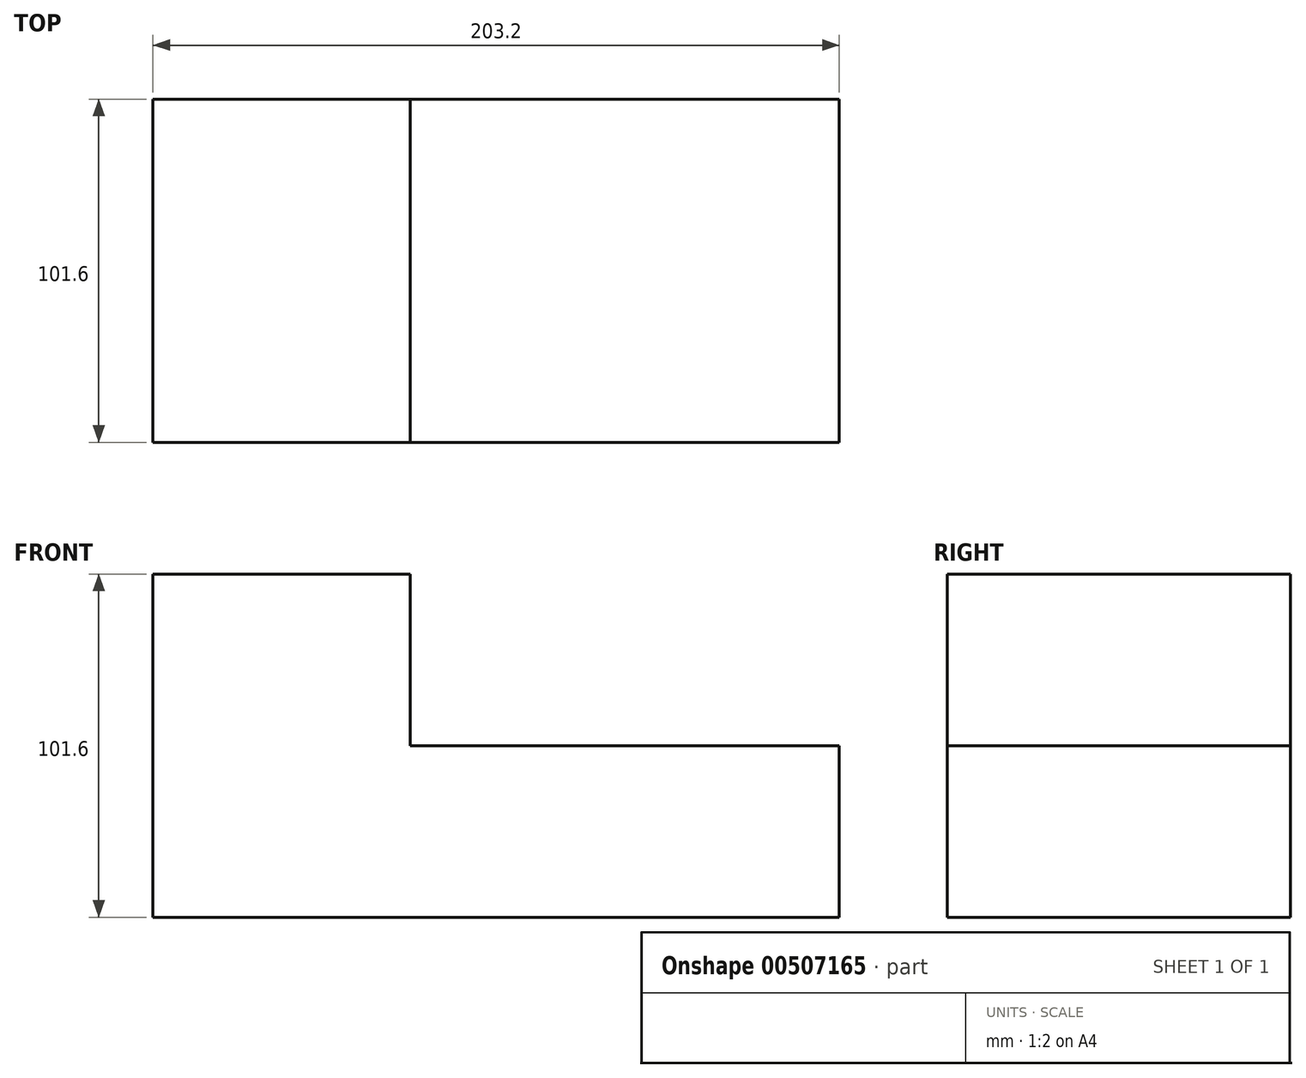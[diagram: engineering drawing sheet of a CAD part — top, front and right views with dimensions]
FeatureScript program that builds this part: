
annotation { "Feature Type Name" : "Feature", "Feature Type Description" : "" }
export const myFeature = defineFeature(function(context is Context, id is Id, definition is map)
    precondition{}
    {
        {
            var Q0;
            Q0=qCreatedBy(makeId("Front.planeOp"),FACE);
            var sketch = newSketch(context, id + "F0", { "sketchPlane" : qUnion([Q0])});
            skLineSegment(sketch, "E0", {"start": v(-76.2, 37.75) * mm, "end": v(0, 37.75) * mm});
            skLineSegment(sketch, "E1", {"start": v(0, 37.75) * mm, "end": v(0, -13.05) * mm});
            skLineSegment(sketch, "E2", {"start": v(0, -13.05) * mm, "end": v(127, -13.05) * mm});
            skLineSegment(sketch, "E3", {"start": v(127, -13.05) * mm, "end": v(127, -63.85) * mm});
            skLineSegment(sketch, "E4", {"start": v(127, -63.85) * mm, "end": v(-76.2, -63.85) * mm});
            skLineSegment(sketch, "E5", {"start": v(-76.2, -63.85) * mm, "end": v(-76.2, 37.75) * mm});
            skSolve(sketch);
        }
        {
            var Q0;
            Q0 = qSketchRegion(id + "F0", true);
            extrude(context, id + "F1", {"entities" : qUnion([Q0]), "depth" : 101.6 * mm});
        }
    });
